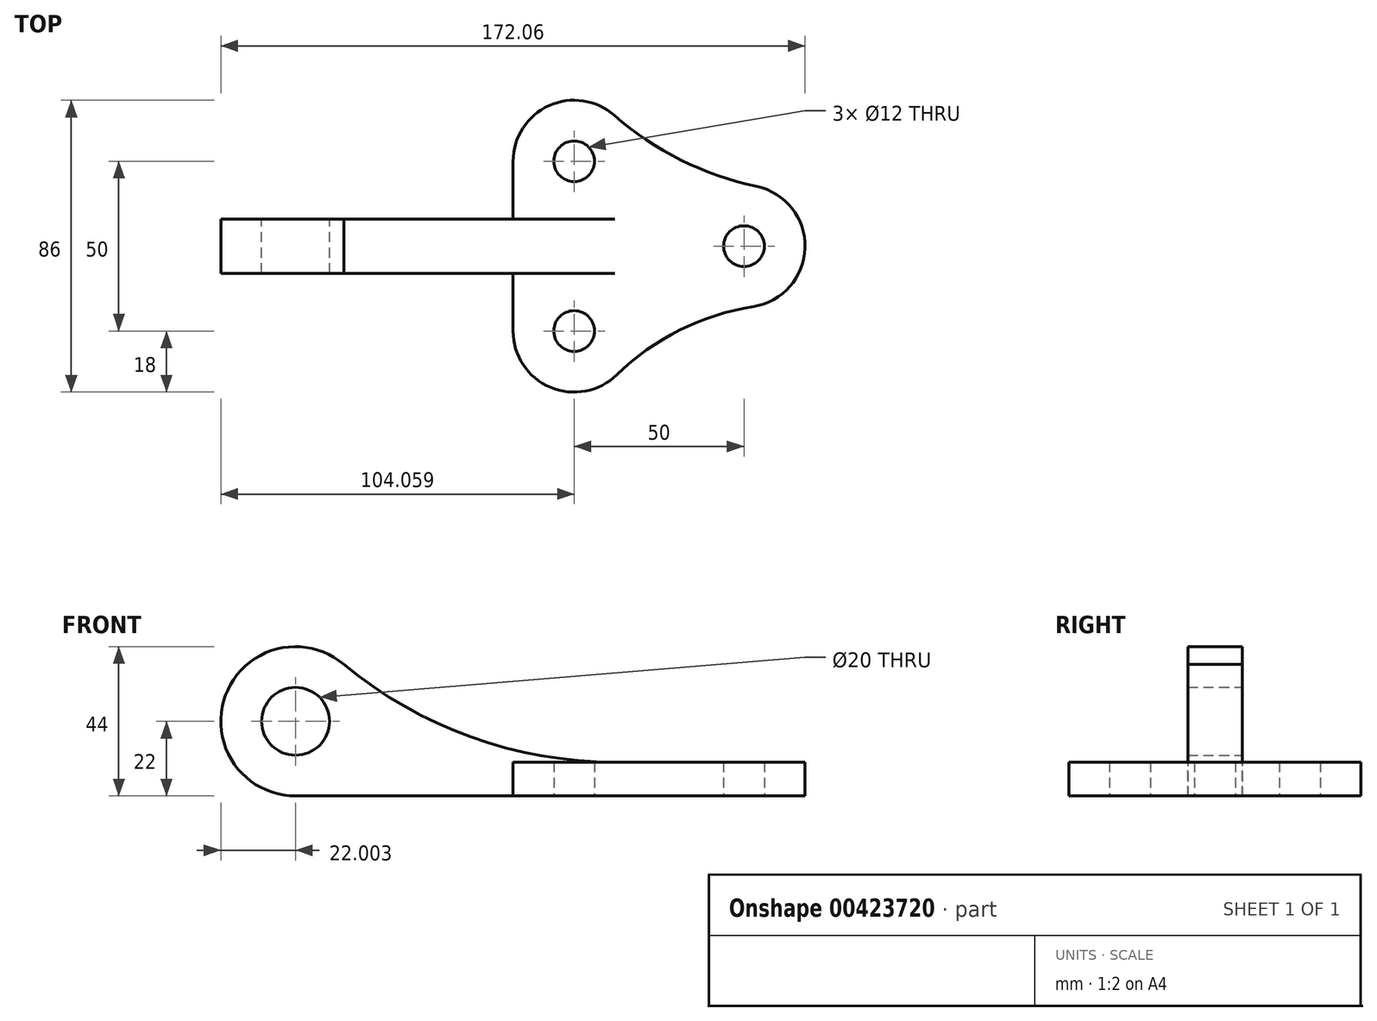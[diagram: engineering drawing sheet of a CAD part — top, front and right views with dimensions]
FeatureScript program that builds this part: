
annotation { "Feature Type Name" : "Feature", "Feature Type Description" : "" }
export const myFeature = defineFeature(function(context is Context, id is Id, definition is map)
    precondition{}
    {
        {
            var Q0;
            Q0=qCreatedBy(makeId("Top.planeOp"),FACE);
            var sketch = newSketch(context, id + "F0", { "sketchPlane" : qUnion([Q0])});
            skCircle(sketch, "E0", {"center": v(11.98, 25) * mm, "radius": 6 * mm});
            skArc(sketch, "E1", {"start": v(23.85, 38.53) * mm, "mid": v(4.55, 41.4) * mm, "end": v(-6.02, 25) * mm});
            skCircle(sketch, "E2", {"center": v(11.98, -25) * mm, "radius": 6 * mm});
            skArc(sketch, "E3", {"start": v(-6.02, -25) * mm, "mid": v(4.98, -41.59) * mm, "end": v(24.54, -37.9) * mm});
            skLineSegment(sketch, "E4", {"start": v(-6.02, 25) * mm, "end": v(-6.02, -25) * mm});
            skLineSegment(sketch, "E5", {"start": v(-76.44, 0) * mm, "end": v(127.02, 0) * mm, "construction": true});
            skCircle(sketch, "E6", {"center": v(61.98, 0) * mm, "radius": 6 * mm});
            skArc(sketch, "E7", {"start": v(64.75, -17.78) * mm, "mid": v(79.97, -0.47) * mm, "end": v(65.68, 17.61) * mm});
            skArc(sketch, "E8", {"start": v(23.85, 38.53) * mm, "mid": v(43.42, 25.38) * mm, "end": v(65.68, 17.61) * mm});
            skArc(sketch, "E9", {"start": v(64.75, -17.78) * mm, "mid": v(43.08, -24.7) * mm, "end": v(24.54, -37.9) * mm});
            skSolve(sketch);
        }
        {
            var Q0;
            Q0=qCreatedBy(makeId("Front.planeOp"),FACE);
            var sketch = newSketch(context, id + "F1", { "sketchPlane" : qUnion([Q0])});
            skCircle(sketch, "E10", {"center": v(-70.08, 22) * mm, "radius": 10 * mm});
            skArc(sketch, "E11", {"start": v(-55.79, 38.73) * mm, "mid": v(-90.72, 29.62) * mm, "end": v(-70.08, 0) * mm});
            skLineSegment(sketch, "E12", {"start": v(-70.08, 0) * mm, "end": v(23.94, 0) * mm});
            skLineSegment(sketch, "E13", {"start": v(23.94, 0) * mm, "end": v(23.94, 10) * mm});
            skLineSegment(sketch, "E14", {"start": v(23.94, 10) * mm, "end": v(-114.93, 10) * mm, "construction": true});
            skArc(sketch, "E15", {"start": v(-55.79, 38.73) * mm, "mid": v(-18.43, 17.4) * mm, "end": v(23.94, 10) * mm});
            skLineSegment(sketch, "E16", {"start": v(39.92, 0) * mm, "end": v(39.92, 5.8) * mm, "construction": true});
            skSolve(sketch);
        }
        {
            var Q0;
            Q0=makeQuery(id+"F1.imprint","IMPRINT",FACE,{"disambiguationData":[TD([[makeQuery(id+"F1.imprint","IMPRINT",EDGE,{"derivedFrom":sQuery(id+"F1.wireOp",EDGE,"E10")}),-1.0]])]});
            extrude(context, id + "F2", {"entities" : qUnion([Q0]), "depth" : 8 * mm, "hasSecondDirection" : true, "secondDirectionOppositeDirection" : true, "secondDirectionDepth" : 8 * mm});
        }
        {
            var Q0;
            Q0=makeQuery(id+"F0.imprint","IMPRINT",FACE,{"disambiguationData":[TD([[makeQuery(id+"F0.imprint","IMPRINT",EDGE,{"derivedFrom":sQuery(id+"F0.wireOp",EDGE,"E0")}),-1.0]])]});
            extrude(context, id + "F3", {"entities" : qUnion([Q0]), "operationType" : NewBodyOperationType.ADD, "depth" : 10 * mm, "hasSecondDirection" : true, "secondDirectionOppositeDirection" : true, "secondDirectionDepth" : 0 * mm});
        }
    });
